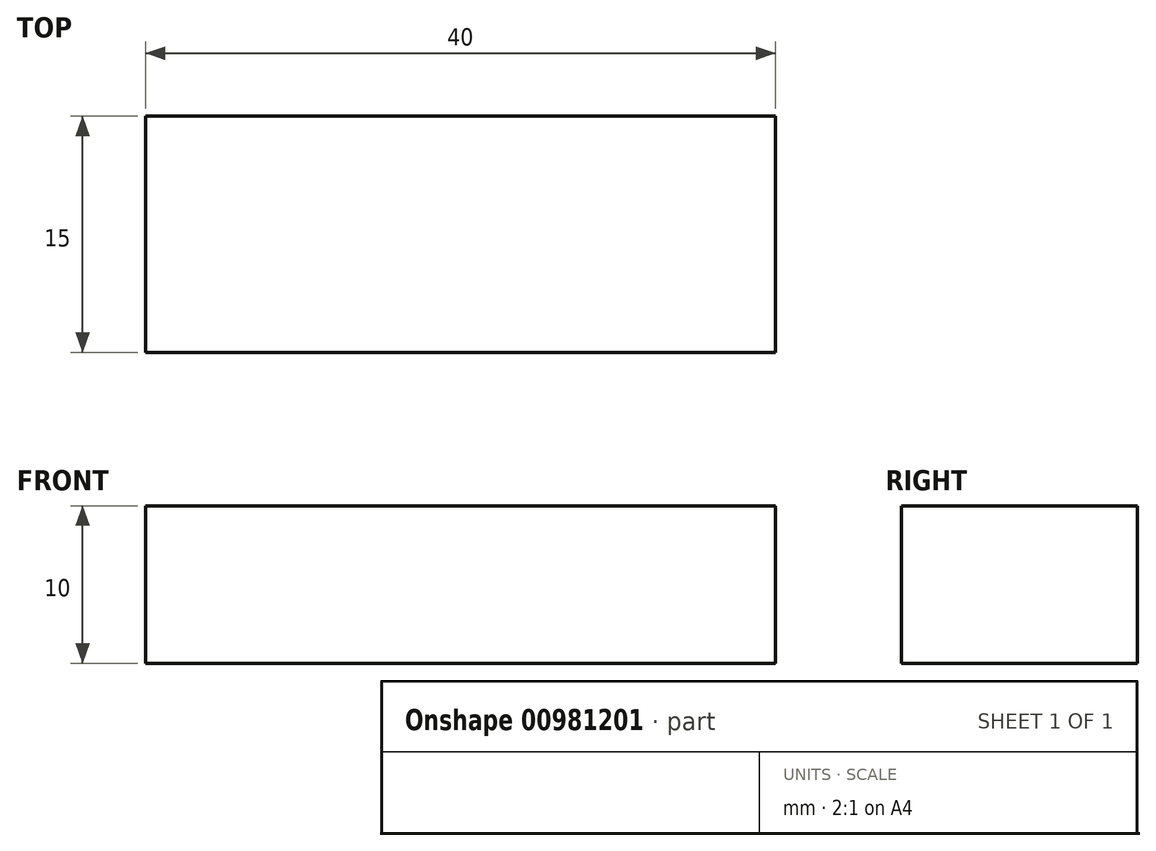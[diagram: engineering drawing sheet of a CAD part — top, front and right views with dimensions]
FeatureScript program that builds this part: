
annotation { "Feature Type Name" : "Feature", "Feature Type Description" : "" }
export const myFeature = defineFeature(function(context is Context, id is Id, definition is map)
    precondition{}
    {
        {
            var Q0;
            Q0=qCreatedBy(makeId("Top.planeOp"),FACE);
            var sketch = newSketch(context, id + "F0", { "sketchPlane" : qUnion([Q0])});
            skLineSegment(sketch, "E0.bottom", {"start": v(0, 0) * mm, "end": v(40, 0) * mm});
            skLineSegment(sketch, "E0.top", {"start": v(0, 15) * mm, "end": v(40, 15) * mm});
            skLineSegment(sketch, "E0.left", {"start": v(0, 0) * mm, "end": v(0, 15) * mm});
            skLineSegment(sketch, "E0.right", {"start": v(40, 0) * mm, "end": v(40, 15) * mm});
            skSolve(sketch);
        }
        {
            var Q0;
            Q0=makeQuery(id+"F0.imprint","IMPRINT",FACE,{"disambiguationData":[TD([[makeQuery(id+"F0.imprint","IMPRINT",EDGE,{"derivedFrom":sQuery(id+"F0.wireOp",EDGE,"E0.bottom")}),1.0]])]});
            extrude(context, id + "F1", {"entities" : qUnion([Q0]), "depth" : 10 * mm, "offsetDistance" : 25 * mm});
        }
    });
